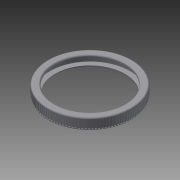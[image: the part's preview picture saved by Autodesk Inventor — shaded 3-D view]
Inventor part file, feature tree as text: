
AUTODESK INVENTOR PART (.ipt)
format: ipt  version: 2014 (Build 180170000, 170)  size: 626,176 bytes
history: native  units: mm
features: extrude x2, fillet x2, sketch x2, plane x1, shell x1, pattern_circular x1
ambient origin geometry x8: Origin, YZ Plane, XZ Plane, XY Plane, X Axis, Y Axis, Z Axis, Center Point
bodies: Volumenkörper1 (feature_tree)
feature tree (9):
  extrude  "Extrusion1"  Depth=8.0mm
  plane  "Arbeitsebene3"
  shell  "Hülle1"  Thickness=8.0mm
  extrude  "Extrusion3"  Depth=1.0mm
  pattern_circular  "Runde Anordnung1"  [2 undecoded]
  fillet  "Rundung1"  Radius=6.0mm
  fillet  "Rundung2"  Radius=0.5mm
  sketch  "Skizze1"  dims[d0=60.0mm d1=50.0mm d2=8.0mm d3=0.0mm]
  sketch  "Skizze4"  dims[d4=1.5mm d5=1.0mm d11=1.0mm d12=6.0mm d13=0.0mm d14=0.5mm d15=1100.0mm d16=360.0deg d18=1.0mm]
note: 2 required parameter values undecoded (feature->parameter linkage not recoverable at this tier; creation-order binding heuristic only, values carry confidence <= 0.55)
